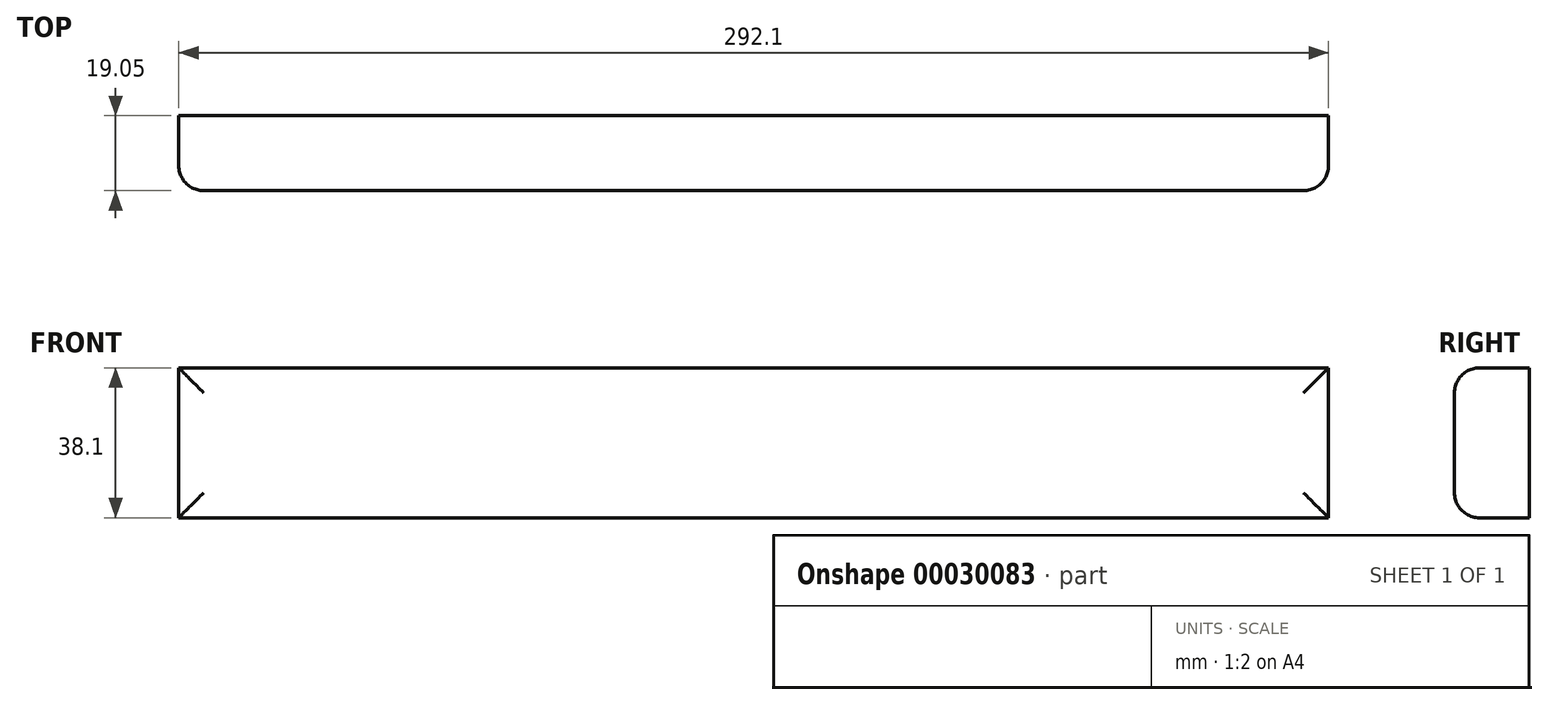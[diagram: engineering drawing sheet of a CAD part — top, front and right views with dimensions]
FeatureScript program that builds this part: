
annotation { "Feature Type Name" : "Feature", "Feature Type Description" : "" }
export const myFeature = defineFeature(function(context is Context, id is Id, definition is map)
    precondition{}
    {
        {
            var Q0;
            Q0=qCreatedBy(makeId("Front.planeOp"),FACE);
            var sketch = newSketch(context, id + "F0", { "sketchPlane" : qUnion([Q0])});
            skLineSegment(sketch, "E0", {"start": v(0, 0) * mm, "end": v(292.1, 0) * mm});
            skLineSegment(sketch, "E1", {"start": v(292.1, 0) * mm, "end": v(292.1, 38.1) * mm});
            skLineSegment(sketch, "E2", {"start": v(292.1, 38.1) * mm, "end": v(0, 38.1) * mm});
            skLineSegment(sketch, "E3", {"start": v(0, 38.1) * mm, "end": v(0, 0) * mm});
            skSolve(sketch);
        }
        {
            var Q0;
            Q0=makeQuery(id+"F0.imprint","IMPRINT",FACE,{"disambiguationData":[TD([[makeQuery(id+"F0.imprint","IMPRINT",EDGE,{"derivedFrom":sQuery(id+"F0.wireOp",EDGE,"E0")}),1.0]])]});
            extrude(context, id + "F1", {"entities" : qUnion([Q0]), "depth" : 19.05 * mm});
        }
        {
            var Q0;
            Q0=makeQuery(id+"F1.opExtrude","CAP_EDGE",EDGE,{"disambiguationData":[OSD([sQuery(id+"F0.wireOp",EDGE,"E2")])],"isStart":false});
            var Q1;
            Q1=makeQuery(id+"F1.opExtrude","CAP_EDGE",EDGE,{"disambiguationData":[OSD([sQuery(id+"F0.wireOp",EDGE,"E3")])],"isStart":false});
            var Q2;
            Q2=makeQuery(id+"F1.opExtrude","CAP_EDGE",EDGE,{"disambiguationData":[OSD([sQuery(id+"F0.wireOp",EDGE,"E0")])],"isStart":false});
            var Q3;
            Q3=makeQuery(id+"F1.opExtrude","CAP_EDGE",EDGE,{"disambiguationData":[OSD([sQuery(id+"F0.wireOp",EDGE,"E1")])],"isStart":false});
            fillet(context, id + "F2", {"entities" : qUnion([Q0, Q1, Q2, Q3]), "radius" : 6.35 * mm, "tangentPropagation" : true, "allowEdgeOverflow" : false});
        }
    });
